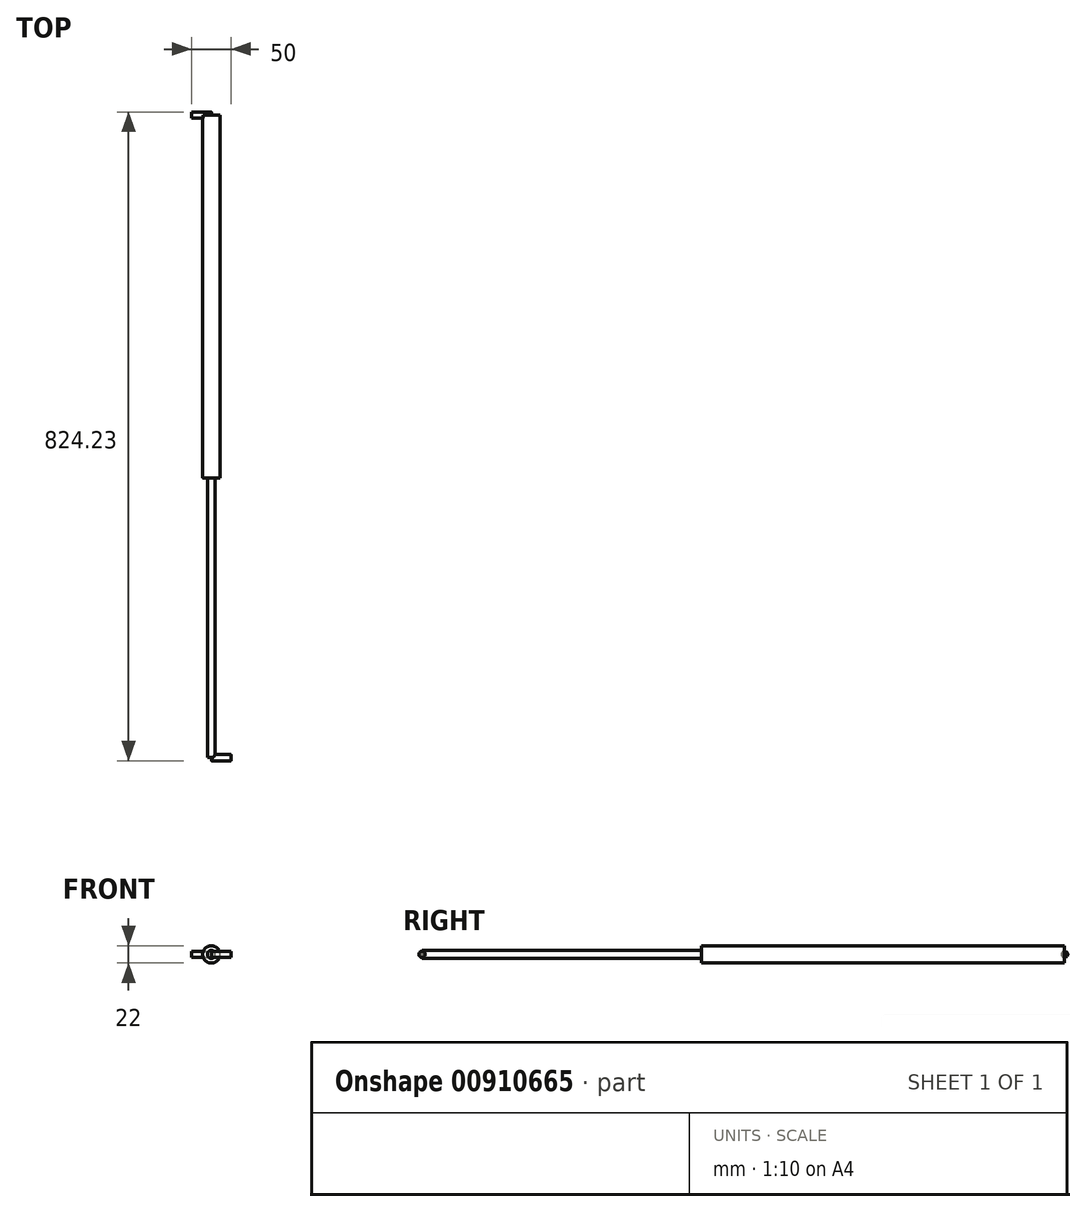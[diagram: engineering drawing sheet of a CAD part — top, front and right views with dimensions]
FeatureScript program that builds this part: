
annotation { "Feature Type Name" : "Feature", "Feature Type Description" : "" }
export const myFeature = defineFeature(function(context is Context, id is Id, definition is map)
    precondition{}
    {
        {
            var Q0;
            Q0=qCreatedBy(makeId("Front.planeOp"),FACE);
            var sketch = newSketch(context, id + "F0", { "sketchPlane" : qUnion([Q0])});
            skCircle(sketch, "E0", {"center": v(0, 0) * mm, "radius": 11 * mm});
            skSolve(sketch);
        }
        {
            var Q0;
            Q0 = qSketchRegion(id + "F0", true);
            extrude(context, id + "F1", {"entities" : qUnion([Q0]), "depth" : 461 * mm, "offsetDistance" : 25 * mm});
        }
        {
            var Q0;
            Q0=makeQuery(id+"F1.opExtrude","CAP_FACE",FACE,{"disambiguationData":[OSD([sQuery(id+"F0.wireOp",EDGE,"E0")])],"isStart":false});
            var sketch = newSketch(context, id + "F2", { "sketchPlane" : qUnion([Q0])});
            skCircle(sketch, "E1", {"center": v(0, 0) * mm, "radius": 5 * mm});
            skSolve(sketch);
        }
        {
            var Q0;
            Q0 = qSketchRegion(id + "F2", true);
            extrude(context, id + "F3", {"entities" : qUnion([Q0]), "depth" : 355 * mm, "offsetDistance" : 25 * mm});
        }
        {
            var Q0;
            Q0=qCreatedBy(makeId("Right.planeOp"),FACE);
            var sketch = newSketch(context, id + "F4", { "sketchPlane" : qUnion([Q0])});
            skCircle(sketch, "E2", {"center": v(-816.23, 0) * mm, "radius": 4 * mm});
            skSolve(sketch);
        }
        {
            var Q0;
            Q0 = qSketchRegion(id + "F4", true);
            extrude(context, id + "F5", {"entities" : qUnion([Q0]), "operationType" : NewBodyOperationType.ADD, "depth" : 25 * mm, "offsetDistance" : 25 * mm});
        }
        {
            var Q0;
            Q0=qCreatedBy(makeId("Right.planeOp"),FACE);
            var sketch = newSketch(context, id + "F6", { "sketchPlane" : qUnion([Q0])});
            skCircle(sketch, "E3", {"center": v(0, 0) * mm, "radius": 4 * mm});
            skSolve(sketch);
        }
        {
            var Q0;
            Q0 = qSketchRegion(id + "F6", true);
            extrude(context, id + "F7", {"entities" : qUnion([Q0]), "operationType" : NewBodyOperationType.ADD, "oppositeDirection" : true, "depth" : 25 * mm, "offsetDistance" : 25 * mm});
        }
    });
